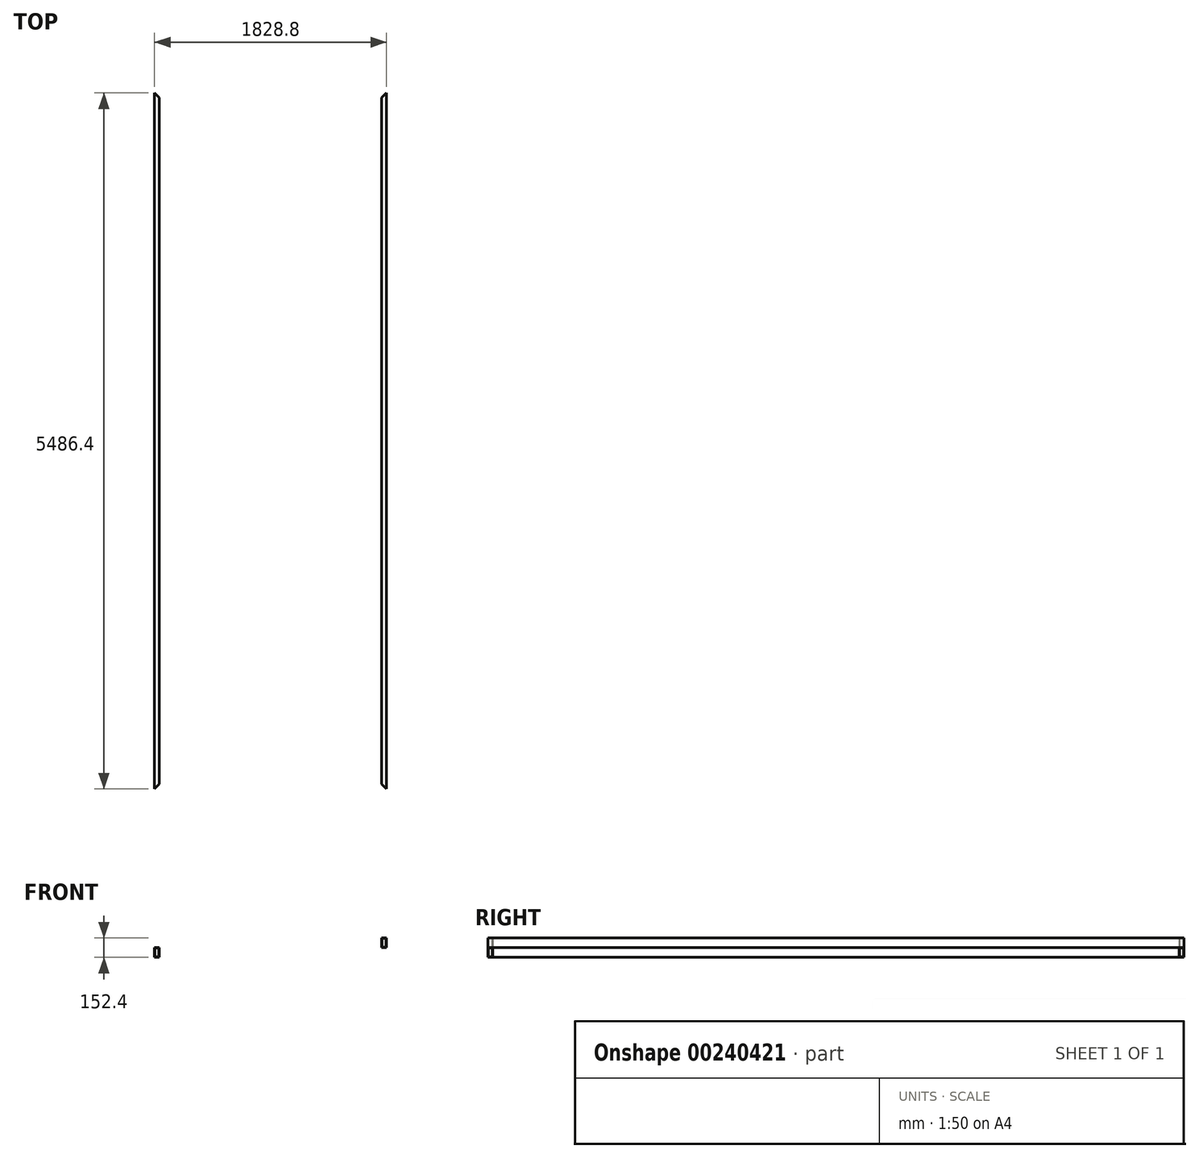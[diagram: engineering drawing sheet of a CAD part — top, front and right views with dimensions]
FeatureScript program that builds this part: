
annotation { "Feature Type Name" : "Feature", "Feature Type Description" : "" }
export const myFeature = defineFeature(function(context is Context, id is Id, definition is map)
    precondition{}
    {
        {
            var Q0;
            Q0=qCreatedBy(makeId("Front.planeOp"),FACE);
            var sketch = newSketch(context, id + "F0", { "sketchPlane" : qUnion([Q0])});
            skLineSegment(sketch, "E0.bottom", {"start": v(-4840.7, 2097.37) * mm, "end": v(-4802.6, 2097.37) * mm});
            skLineSegment(sketch, "E0.top", {"start": v(-4840.7, 2021.17) * mm, "end": v(-4802.6, 2021.17) * mm});
            skLineSegment(sketch, "E0.left", {"start": v(-4840.7, 2097.37) * mm, "end": v(-4840.7, 2021.17) * mm});
            skLineSegment(sketch, "E0.right", {"start": v(-4802.6, 2097.37) * mm, "end": v(-4802.6, 2021.17) * mm});
            skSolve(sketch);
        }
        {
            var Q0;
            Q0 = qSketchRegion(id + "F0", true);
            extrude(context, id + "F1", {"entities" : qUnion([Q0]), "depth" : 5486.4 * mm});
        }
        {
            var Q0;
            Q0=makeQuery(id+"F1.opExtrude","CAP_FACE",FACE,{"disambiguationData":[OSD([sQuery(id+"F0.wireOp",EDGE,"E0.bottom"),sQuery(id+"F0.wireOp",EDGE,"E0.top"),sQuery(id+"F0.wireOp",EDGE,"E0.left"),sQuery(id+"F0.wireOp",EDGE,"E0.right")])],"isStart":false});
            shell(context, id + "F2", {"entities" : qUnion([Q0]), "thickness" : 3.17 * mm});
        }
        {
            var Q0;
            Q0=makeQuery(id+"F1.opExtrude","SWEPT_FACE",FACE,{"disambiguationData":[OSD([sQuery(id+"F0.wireOp",EDGE,"E0.bottom")])]});
            var sketch = newSketch(context, id + "F3", { "sketchPlane" : qUnion([Q0])});
            skLineSegment(sketch, "E1", {"start": v(-4840.7, -5486.4) * mm, "end": v(-4802.6, -5448.3) * mm});
            skLineSegment(sketch, "E2", {"start": v(-4802.6, -5448.3) * mm, "end": v(-4802.6, -5486.4) * mm});
            skLineSegment(sketch, "E3", {"start": v(-4802.6, -5486.4) * mm, "end": v(-4840.7, -5486.4) * mm});
            skSolve(sketch);
        }
        {
            var Q0;
            Q0 = qSketchRegion(id + "F3", true);
            extrude(context, id + "F4", {"entities" : qUnion([Q0]), "operationType" : NewBodyOperationType.REMOVE, "endBound" : BoundingType.THROUGH_ALL, "oppositeDirection" : true, "depth" : 25.4 * mm});
        }
        {
            var Q0;
            Q0=makeQuery(id+"F1.opExtrude","SWEPT_FACE",FACE,{"disambiguationData":[OSD([sQuery(id+"F0.wireOp",EDGE,"E0.bottom")])]});
            var sketch = newSketch(context, id + "F5", { "sketchPlane" : qUnion([Q0])});
            skLineSegment(sketch, "E4", {"start": v(-4840.7, 0) * mm, "end": v(-4802.6, 0) * mm});
            skLineSegment(sketch, "E5", {"start": v(-4802.6, 0) * mm, "end": v(-4802.6, -38.1) * mm});
            skLineSegment(sketch, "E6", {"start": v(-4802.6, -38.1) * mm, "end": v(-4840.7, 0) * mm});
            skSolve(sketch);
        }
        {
            var Q0;
            Q0 = qSketchRegion(id + "F5", true);
            extrude(context, id + "F6", {"entities" : qUnion([Q0]), "operationType" : NewBodyOperationType.REMOVE, "endBound" : BoundingType.THROUGH_ALL, "oppositeDirection" : true, "depth" : 25.4 * mm});
        }
        {
            var Q0;
            Q0=makeQuery(id+"F1.opExtrude","SWEPT_BODY",BODY,{"disambiguationData":[OSD([sQuery(id+"F0.wireOp",EDGE,"E0.bottom"),sQuery(id+"F0.wireOp",EDGE,"E0.top"),sQuery(id+"F0.wireOp",EDGE,"E0.left"),sQuery(id+"F0.wireOp",EDGE,"E0.right")])]});
            transform(context, id + "F7", {"entities" : qUnion([Q0]), "transformType" : TransformType.TRANSLATION_3D, "dx" : 1828.8 * mm, "dy" : 0 * mm, "dz" : 0 * mm, "makeCopy" : true});
        }
        {
            var Q0;
            Q0=makeQuery(id+"F7.opPattern","COPY",BODY,{"derivedFrom":makeQuery(id+"F1.opExtrude","SWEPT_BODY",BODY,{"disambiguationData":[OSD([sQuery(id+"F0.wireOp",EDGE,"E0.bottom"),sQuery(id+"F0.wireOp",EDGE,"E0.top"),sQuery(id+"F0.wireOp",EDGE,"E0.left"),sQuery(id+"F0.wireOp",EDGE,"E0.right")])]}),"instanceName":"1"});
            var Q1;
            Q1=makeQuery(id+"F7.opPattern","COPY",EDGE,{"derivedFrom":makeQuery(id+"F1.opExtrude","SWEPT_EDGE",EDGE,{"disambiguationData":[OSD([sQuery(id+"F0.wireOp",EDGE,"E0.bottom"),sQuery(id+"F0.wireOp",EDGE,"E0.left")])]}),"instanceName":"1"});
            transform(context, id + "F8", {"entities" : qUnion([Q0]), "transformType" : TransformType.ROTATION, "transformAxis" : qUnion([Q1]), "angle" : 180 * degree, "makeCopy" : false});
        }
    });
